# Revit family: Plastic channel Base DN100 with a high board
name_source: partatom
category: Оборудование
units: mm (PartAtom-declared; Revit-internal decimal feet)

## family parameters
Общий = Да
Основа = Грань
При загрузке вырезать с полостями = Нет
Размер круглого соединителя = Использовать диаметр
Тип детали = Нормальный
Точка расчета площади = Нет

## types (19) — shared parameters
A01 = plastic mesh : 208011
A02 = plastic mesh : 208021
A03 = plastic mesh ADA : 208012
A04 = plastic mesh ADA : 208022
A05 = plastic mesh ADA : 208032
ADSK_Dimension_Diameter = 100 мм
ADSK_Dimension_Lenght = 1000 мм
ADSK_Dimension_Width = 160 мм
ADSK_Load class = C250
ADSK_Manufacturer = Vodaland
ADSK_Material_Name = Plastic
ADSK_Unit = pcs
Cap1 = Plastic end cap Base DN100 : 630-1
Cap2 = Plastic end cap Base DN100 : 630-2
Cap3 = Plastic end cap Base DN100 : 630-3
Cap8010 = Plastic end cap Base DN100 : 630080
Cap8020 = Plastic end cap Base DN100 : 630120
Cap8050 = Plastic end cap Base DN100 : 630060
Co1 = Plastic end cap with outlet Base DN100 : 6308-1
Co2 = Plastic end cap with outlet Base DN100 : 6308-2
Co3 = Plastic end cap with outlet Base DN100 : 6308-3
Co4 = Plastic end cap with outlet Base DN100 : 6308-4
Co8050 = Plastic end cap with outlet Base DN100 : 6300608
Co805050 = Plastic end cap with outlet Base DN100 : 6300608-50
Connector = Plastic end cap with outlet Base DN100 : 6308-1
Fa1 = Choice of fastening : 6100-35
Fa2 = Choice of fastening : 6200-35
Fr1 = Fastening : 6100-35
Fr2 = Fastening : 6200-35
Fr3 = Fastening : 6800-35
G01 = Plastic grate Base DN100 mesh : 208011
G02 = Plastic grate Base DN100 mesh : 208021
G03 = Plastic grate Base DN100 mesh ADA : 208012
G04 = Plastic grate Base DN100 mesh ADA : 208022
G05 = Plastic grate Base DN100 mesh ADA : 208032
W1 = 160 мм
W2 = 156 мм
bias = Нет
la = Да
no = No : ні
Группа модели = Linear drainage
zero-valued in all types: Отметка по умолчанию

## per-type parameters (varying)
| type | ADSK_Dimension_Height | ADSK_Name | ADSK_Sealant | ADSK_Weight | CN | Cap_begin | Cap_end | H1 | H2 | R1 | R2 |
| 80061 | 75 мм | Plastic channel Base DN100 H75 with a high board | 10 | 1.2 | 8050 | Plastic end cap Base DN100 : 630060 | Plastic end cap Base DN100 : 630060 | 35 мм | 35 мм | 5 мм | 5 мм |
| 80081-1 | 95 мм | Plastic slope channel Base DN100 H95 1 with a high board | 11 | 1.4 | 80080 | Plastic end cap Base DN100 : 630060 | Plastic end cap Base DN100 : 630-1 | 55 мм | 55 мм | 5 мм | 25 мм |
| 80081 | 95 мм | Plastic channel Base DN100 H95 with a high board | 11 | 1.2 | 8010 | Plastic end cap Base DN100 : 630080 | Plastic end cap Base DN100 : 630080 | 55 мм | 55 мм | 25 мм | 25 мм |
| 80091-2 | 105 мм | Plastic slope channel Base DN100 H105 2 with a high board | 11 | 1.4 | 80090 | Plastic end cap Base DN100 : 630-1 | Plastic end cap Base DN100 : 630-1 | 65 мм | 65 мм | 25 мм | 25 мм |
| 80101-3 | 115 мм | Plastic slope channel Base DN100 H115 3 with a high board | 12 | 1.5 | 80100 | Plastic end cap Base DN100 : 630-1 | Plastic end cap Base DN100 : 630-2 | 75 мм | 75 мм | 25 мм | 49 мм |
| 80101 | 115 мм | Plastic channel Base DN100 H115 with a high board | 12 | 1.4 | 80100 | Plastic end cap Base DN100 : 630-1 | Plastic end cap Base DN100 : 630-2 | 75 мм | 75 мм | 49 мм | 49 мм |
| 80111-4 | 125 мм | Plastic slope channel Base DN100 H125 4 with a high board | 12 | 1.7 | 80110 | Plastic end cap Base DN100 : 630-2 | Plastic end cap Base DN100 : 630-2 | 85 мм | 85 мм | 49 мм | 49 мм |
| 80121-5 | 135 мм | Plastic slope channel Base DN100 H135 5 with a high board | 13 | 1.8 | 80120 | Plastic end cap Base DN100 : 630-2 | Plastic end cap Base DN100 : 630-2 | 95 мм | 95 мм | 49 мм | 49 мм |
| 80121 | 135 мм | Plastic channel Base DN100 H135 with a high board | 13 | 1.8 | 8020 | Plastic end cap Base DN100 : 630120 | Plastic end cap Base DN100 : 630120 | 95 мм | 95 мм | 49 мм | 49 мм |
| 80131-6 | 145 мм | Plastic slope channel Base DN100 H145 6 with a high board | 14 | 1.8 | 80130 | Plastic end cap Base DN100 : 630-2 | Plastic end cap Base DN100 : 630-2 | 105 мм | 105 мм | 49 мм | 49 мм |
| 80141-7 | 155 мм | Plastic slope channel Base DN100 H155 7 with a high board | 14 | 1.9 | 80140 | Plastic end cap Base DN100 : 630-2 | Plastic end cap Base DN100 : 630-2 | 115 мм | 115 мм | 49 мм | 49 мм |
| 80151-8 | 165 мм | Plastic slope channel Base DN100 H165 8 with a high board | 16 | 2 | 80150 | Plastic end cap Base DN100 : 630-2 | Plastic end cap Base DN100 : 630-2 | 125 мм | 125 мм | 49 мм | 49 мм |
| 80151 | 165 мм | Plastic channel Base DN100 H165 with a high board | 16 | 2.1 | 8000 | Plastic end cap Base DN100 : 630-2 | Plastic end cap Base DN100 : 630-2 | 125 мм | 125 мм | 49 мм | 49 мм |
| 80161-9 | 175 мм | Plastic slope channel Base DN100 H175 9 with a high board | 17 | 2.1 | 80160 | Plastic end cap Base DN100 : 630-2 | Plastic end cap Base DN100 : 630-3 | 135 мм | 135 мм | 49 мм | 49 мм |
| 80171-10 | 185 мм | Plastic slope channel Base DN100 H185 10 with a high board | 18 | 2.2 | 80170 | Plastic end cap Base DN100 : 630-3 | Plastic end cap Base DN100 : 630-3 | 145 мм | 145 мм | 49 мм | 49 мм |
| 80181-11 | 195 мм | Plastic slope channel Base DN100 H195 11 with a high board | 19 | 2.3 | 80180 | Plastic end cap Base DN100 : 630-3 | Plastic end cap Base DN100 : 630-3 | 155 мм | 155 мм | 49 мм | 49 мм |
| 80191-12 | 205 мм | Plastic slope channel Base DN100 H205 12 with a high board | 20 | 2.4 | 80190 | Plastic end cap Base DN100 : 630-3 | Plastic end cap Base DN100 : 630-3 | 165 мм | 165 мм | 49 мм | 49 мм |
| 80201-13 | 215 мм | Plastic slope channel Base DN100 H215 13 with a high board | 21 | 2.5 | 80200 | Plastic end cap Base DN100 : 630-3 | Plastic end cap Base DN100 : 630-3 | 175 мм | 175 мм | 49 мм | 49 мм |
| 80201 | 215 мм | Plastic channel Base DN100 H215 with a high board | 21 | 2.5 | 80200 | Plastic end cap Base DN100 : 630-3 | Plastic end cap Base DN100 : 630-3 | 175 мм | 175 мм | 49 мм | 49 мм |

note: column(s) folded — value = type name in every type: ADSK_Product code

## geometry (parser evidence)
native form markers: Blend x4
no freeform markers — native parametric forms only
